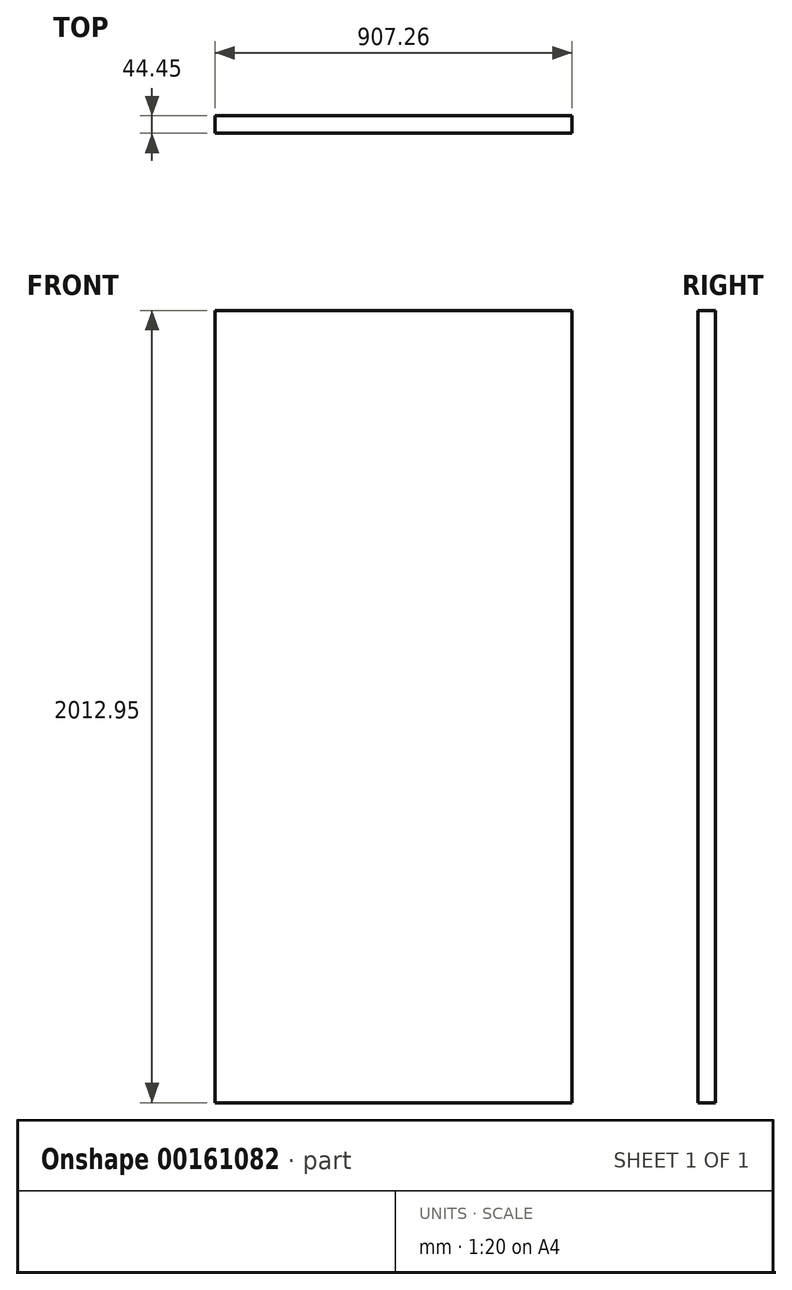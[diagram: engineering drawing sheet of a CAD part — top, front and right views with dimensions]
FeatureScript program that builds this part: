
annotation { "Feature Type Name" : "Feature", "Feature Type Description" : "" }
export const myFeature = defineFeature(function(context is Context, id is Id, definition is map)
    precondition{}
    {
        {
            var Q0;
            Q0=qCreatedBy(makeId("Top.planeOp"),FACE);
            var sketch = newSketch(context, id + "F0", { "sketchPlane" : qUnion([Q0])});
            skLineSegment(sketch, "E0.bottom", {"start": v(0, 0) * mm, "end": v(-907.26, 0) * mm});
            skLineSegment(sketch, "E0.top", {"start": v(0, 44.45) * mm, "end": v(-907.26, 44.45) * mm});
            skLineSegment(sketch, "E0.left", {"start": v(0, 0) * mm, "end": v(0, 44.45) * mm});
            skLineSegment(sketch, "E0.right", {"start": v(-907.26, 0) * mm, "end": v(-907.26, 44.45) * mm});
            skSolve(sketch);
        }
        {
            var Q0;
            Q0=qSketchRegion(id+"F0",true);
            extrude(context, id + "F1", {"entities" : qUnion([Q0]), "depth" : 2012.95 * mm});
        }
    });
